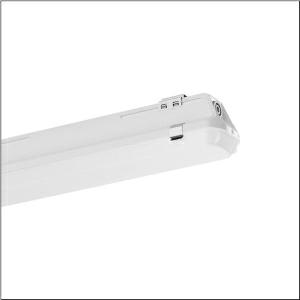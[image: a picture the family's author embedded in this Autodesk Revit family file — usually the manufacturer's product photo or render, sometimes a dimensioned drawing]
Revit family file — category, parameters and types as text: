
# Revit family: monsun_r__21_parking_51fg20dp440bhr_9634
name_source: partatom
category: Lighting Fixtures
units: mm (PartAtom-declared; Revit-internal decimal feet)

## family parameters
Cut with Voids When Loaded = No
Host = Face
Light Source = No
Part Type = Normal
Room Calculation Point = No
Round Connector Dimension = Use Diameter
Shared = No

## types (1)
- --- (1 x LED, 4810 lm, 34.9 W, 4000K)
    Apparent Load = 35 VA
    CIE Flux Codes = 45 75 93 94 100
    Color Rendering = 80
    Color Temperature = 4000K
    Default Elevation = 1800 mm
    Description = Monsun® 21 parking, damp-proof luminaire, chain hanger, primary optical cover: enclosure, of PC, light emission: direct distribution, primary light characteristic: symmetric, installation type: vertical mounting, horizontal mounting, surface-mounted, suspended mounting, LED, rated luminous flux: 4.810lm, luminous efficacy: 140lm/W, light colour: 840, colour temperature: 4000K, control gear: ECG DALI, with terminal, 5-pole, max. 2.5mm², mains connection: 220..240V, AC, 50/60Hz, rated input power: 34W, housing, of glass-fibre reinforced polyester, uncoated, bright grey, incl. chain hanger, length: 1.590mm, width: 90mm, height: 88mm, clip for enclosure, of stainless steel (V2A), ceiling mounting element, of stainless steel (V2A), chain hanger, of stainless steel (V2A), multi-sensor HC1, local control, light sensor deactivated, dimmable, protection rating (complete): IP66, insulation class (complete): insulation class I (protective earthing), certification: CE, ENEC, VDE, UKCA, protection symbol: D, impact resistance: IK08, permissible operating ambient temperature: -25..+35°C, standard: EN 50419, EN 60598-2-1, no direct snow, no direct sun, no direct rain, for indoor or canopied outdoor use, corresponds to IFS (International Featured Standards) requirements for safety and quality in the food industry, contact your sales advisor before using the luminaires in applications with unclear chemical exposure, large temperature fluctuations or condensation-forming humidity, LABS conformity tested according to VDMA 24364:2018-05, packaging unit: 1 piece
    Height = 89 mm
    Lamp = 1 x LED
    Lamp Light Flux = 4810 lm
    Lamp Power = 34.9 W
    Lamp count = 1
    Length = 1590 mm
    Luminous efficacy = 138 lm/W
    Manufacturer = Siteco
    ModVariant = No
    Model = 51FG20DP440BHR
    Mounting Place = Ceiling
    Mounting Type = Surface mounted
    Number of Poles = 1
    OnlyDefault = Yes
    Power Factor = 1
    Product Name = Monsun® 21 parking
    Product group = damp-proof luminaire
    ProductGroupID = 300
    Protection Class = Protection class I
    Protection Degree = IP 66
    RLX_Detail_Level = 1
    RLX_Emergency_Light_Flux = 0 lm
    RLX_Emergency_Type = 0
    RLX_Emergency_Type_DB = No
    RlxData = <blob elided: 92221 chars, md5=346e7e45>
    Socket = socket
    Standby Power = 0 W
    System Light Flux = 4810 lm
    System Power = 35 W
    Type Comments = factory setting: luminous flux: 100 % | dim-lin: 254 | 228 mA
    Type Image = l_1006717.jpg
    URL = http://relux.com
    VarID = @adj_074753
    Voltage = 0 V
    Weight = 0.00 kg
    Width = 90 mm

## geometry (parser evidence)
native form markers: Blend x4, Sweep x15
no freeform markers — native parametric forms only
